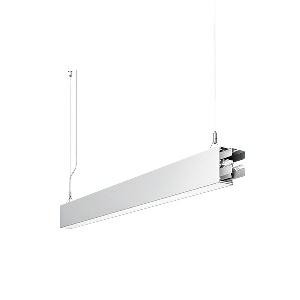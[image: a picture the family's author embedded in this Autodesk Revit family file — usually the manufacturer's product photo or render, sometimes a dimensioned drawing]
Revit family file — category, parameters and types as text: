
# Revit family: dotoo_line_-_dlp_1500_830_d_sta_00805802_139b
name_source: partatom
category: Lighting Fixtures
units: mm (PartAtom-declared; Revit-internal decimal feet)

## family parameters
Cut with Voids When Loaded = No
Host = Face
Light Source = No
Part Type = Normal
Room Calculation Point = No
Round Connector Dimension = Use Diameter
Shared = No

## types (1)
- DOTOO.line - DLP 1500/830/D STA (1 x LED, 1300 lm, 3000K)
    Apparent Load = 13 VA
    Approval mark = CE
    CIE Flux Codes = 67 91 98 100 100
    Color Rendering = 80-89
    Color Temperature = 3000K
    Control Gear = Electronic ballast
    Default Elevation = 1800 mm
    Description = DLP 1500/830/D|Suspended luminaire|light source: LED|connected load: 220-240 V, 50/60 Hz|Power consumption: approx. 13 W|standby: approx. 0,20|luminous flux: 1300 lm|luminous efficacy: 100 lm/W|light distribution: Direct|direct ratio: approx. 100 %|colour temperature: Warm white, ca. 3000 K|color rendering index (CRI): >= 80|chromaticity tolerance:  3 SDCM|System of protection: IP 40|technology: Continuously dimmable|luminaire body|material: Sectional aluminium|colour: White|lamp cover: Acrylic (PMMA), Clear|mains lead: 2.00 m With free stranded wires|Fastening: Steel cable 0.3 - 0.7 m|glare control: Prism aperture|luminance(L65): <= 3000 cd/m|unified glare rating(4H 8H): <=  19|special features: DALI Load 1x, TouchDIM - dimming via standard switch, Through-wired, up to 18 m on one mains connection, Flicker-free, Suitable as emergency lighting, Start luminaire with mains connection, Mechanical and electrical connection of the individual modules without tools|
    Frequency = 50 Hz
    Height = 110 mm
    Lamp = 1 x LED
    Lamp Light Flux = 1300 lm
    Lamp count = 1
    Length = 1128 mm
    Luminous efficacy = 100 lm/W
    Manufacturer = Waldmann
    ModVariant = No
    Model = 00805802
    Mounting Place = Ceiling
    Mounting Type = Pendant
    Number of Poles = 1
    OnlyDefault = Yes
    Power Factor = 1
    Product Name = DOTOO.line - DLP 1500/830/D STA
    Product group = Suspended luminaire
    ProductGroupID = 9
    Protection Class = Protection class I
    Protection Degree = IP 40
    RLX_Detail_Level = 1
    RLX_Emergency_Light_Flux = 0 lm
    RLX_Emergency_Type = 0
    RLX_Emergency_Type_DB = No
    RlxData = <blob elided: 21001 chars, md5=b86f2137>
    Socket = socket
    Standby Power = 0 W
    System Light Flux = 1300 lm
    System Power = 13 W
    Type Comments = Product without accessories
    Type Image = 113301000-00692567.jpg
    URL = http://relux.com
    VarID = ---
    Voltage = 230 V
    Voltage Range = 220-240 V
    Weight = 0.00 kg
    Width = 60 mm  [stored 0.19685 ft]

note: [stored X ft] marks values corroborated as IEEE doubles in the binary element streams (Revit-internal decimal feet)

## geometry (parser evidence)
native form markers: Blend x4, Sweep x12
no freeform markers — native parametric forms only
